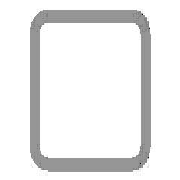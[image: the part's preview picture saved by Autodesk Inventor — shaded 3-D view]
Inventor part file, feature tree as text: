
AUTODESK INVENTOR PART (.ipt)
format: ipt  version: 2025 (Build 290162010, 162A)  size: 133,120 bytes
history: native  units: mm (DEFAULTED — no unit token found)
features: other x4, sketch x1, plane x1
ambient origin geometry x8: Origin, YZ Plane, XZ Plane, XY Plane, X Axis, Y Axis, Z Axis, Center Point
bodies: Solid1 (feature_tree), Body (feature_tree)
feature tree (6):
  parser-record x1  (decoder bookkeeping rows leaked as tree rows — omitted from the tree; the rows remain in map.json)
  other  "Driven Length"
  other  "Start Plane"
  other  "End Plane"
  sketch  "Sketch3"  dims[d3=769.289468mm d4=0.0mm d7=8.0mm d9=50.0mm d11=50.0mm d12=4.0mm d13=-0.0mm d14=769.289468mm d15=25.0mm d16=25.0mm d17=90.0deg d18=769.289468mm]
  plane  "Work Plane3"
